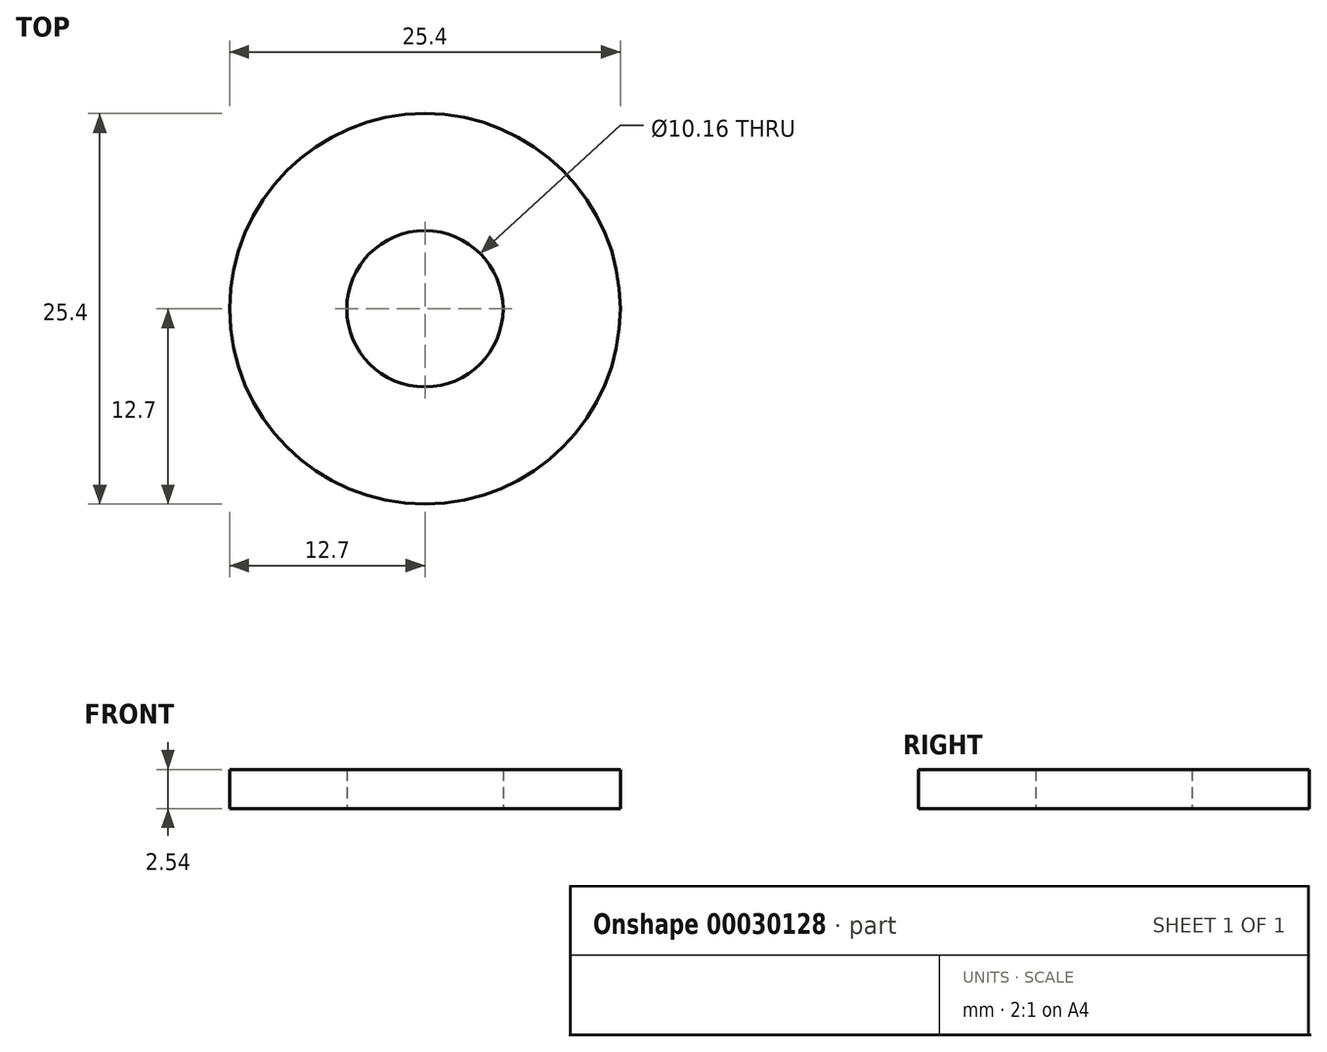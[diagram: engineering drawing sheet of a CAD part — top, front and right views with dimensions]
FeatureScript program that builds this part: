
annotation { "Feature Type Name" : "Feature", "Feature Type Description" : "" }
export const myFeature = defineFeature(function(context is Context, id is Id, definition is map)
    precondition{}
    {
        {
            var Q0;
            Q0=qCreatedBy(makeId("Top.planeOp"),FACE);
            var sketch = newSketch(context, id + "F0", { "sketchPlane" : qUnion([Q0])});
            skCircle(sketch, "E0", {"center": v(0, 0) * mm, "radius": 12.7 * mm});
            skCircle(sketch, "E1", {"center": v(0, 0) * mm, "radius": 5.08 * mm});
            skSolve(sketch);
        }
        {
            var Q0;
            Q0=makeQuery(id+"F0.imprint","IMPRINT",FACE,{"disambiguationData":[TD([[makeQuery(id+"F0.imprint","IMPRINT",EDGE,{"derivedFrom":sQuery(id+"F0.wireOp",EDGE,"E0")}),1.0]])]});
            extrude(context, id + "F1", {"entities" : qUnion([Q0]), "depth" : 2.54 * mm});
        }
    });
